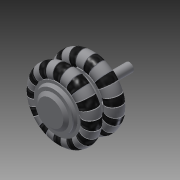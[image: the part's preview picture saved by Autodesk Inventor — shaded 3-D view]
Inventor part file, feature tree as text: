
AUTODESK INVENTOR PART (.ipt)
format: ipt  version: 2015 (Build 190159000, 159)  size: 1,502,208 bytes
history: native  units: in
note: dims shown in document units (in); Inventor stores cm internally (conversion verified against a paired STEP export)
features: sketch x4, other x3, extrude x1
ambient origin geometry x8: Origin, YZ Plane, XZ Plane, XY Plane, X Axis, Y Axis, Z Axis, Center Point
bodies: Solid1 (feature_tree)
feature tree (8):
  other  "omniWheelSet.ipt"
  extrude  "Extrusion1"  Depth=0.0984in TaperAngle=0.0deg
  other  "Solid1::omniWheelSet.ipt"
  other  "TaggingFeature1"
  sketch  "Sketch3"  dims[d0=0.7874in d1=0.0984in d2=0.0in]
  sketch  "Sketch5"
  sketch  "Sketch15"
  sketch  "Sketch6"
